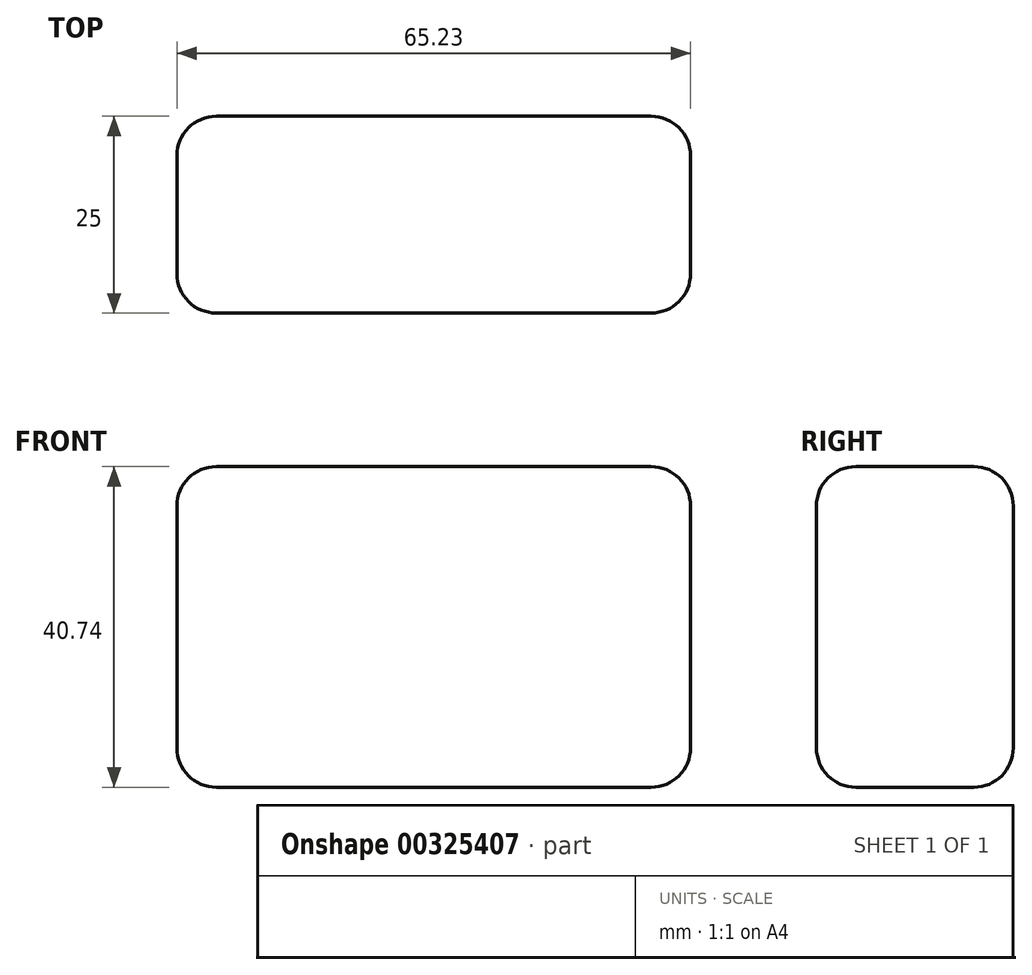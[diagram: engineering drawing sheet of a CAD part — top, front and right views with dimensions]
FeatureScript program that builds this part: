
annotation { "Feature Type Name" : "Feature", "Feature Type Description" : "" }
export const myFeature = defineFeature(function(context is Context, id is Id, definition is map)
    precondition{}
    {
        {
            var Q0;
            Q0=qCreatedBy(makeId("Front.planeOp"),FACE);
            var sketch = newSketch(context, id + "F0", { "sketchPlane" : qUnion([Q0])});
            skLineSegment(sketch, "E0.bottom", {"start": v(18.75, 67.72) * mm, "end": v(83.98, 67.72) * mm});
            skLineSegment(sketch, "E0.top", {"start": v(18.75, 26.98) * mm, "end": v(83.98, 26.98) * mm});
            skLineSegment(sketch, "E0.left", {"start": v(18.75, 67.72) * mm, "end": v(18.75, 26.98) * mm});
            skLineSegment(sketch, "E0.right", {"start": v(83.98, 67.72) * mm, "end": v(83.98, 26.98) * mm});
            skSolve(sketch);
        }
        {
            var Q0;
            Q0=makeQuery(id+"F0.imprint","IMPRINT",FACE,{"disambiguationData":[TD([[makeQuery(id+"F0.imprint","IMPRINT",EDGE,{"derivedFrom":sQuery(id+"F0.wireOp",EDGE,"E0.bottom")}),-1.0]])]});
            extrude(context, id + "F1", {"entities" : qUnion([Q0]), "depth" : 25 * mm});
        }
        {
            var Q0;
            Q0=makeQuery(id+"F1.opExtrude","CAP_FACE",FACE,{"disambiguationData":[OSD([sQuery(id+"F0.wireOp",EDGE,"E0.bottom"),sQuery(id+"F0.wireOp",EDGE,"E0.top"),sQuery(id+"F0.wireOp",EDGE,"E0.left"),sQuery(id+"F0.wireOp",EDGE,"E0.right")])],"isStart":false});
            var Q1;
            Q1=makeQuery(id+"F1.opExtrude","SWEPT_FACE",FACE,{"disambiguationData":[OSD([sQuery(id+"F0.wireOp",EDGE,"E0.bottom")])]});
            var Q2;
            Q2=makeQuery(id+"F1.opExtrude","CAP_FACE",FACE,{"disambiguationData":[OSD([sQuery(id+"F0.wireOp",EDGE,"E0.bottom"),sQuery(id+"F0.wireOp",EDGE,"E0.top"),sQuery(id+"F0.wireOp",EDGE,"E0.left"),sQuery(id+"F0.wireOp",EDGE,"E0.right")])],"isStart":true});
            var Q3;
            Q3=makeQuery(id+"F1.opExtrude","SWEPT_FACE",FACE,{"disambiguationData":[OSD([sQuery(id+"F0.wireOp",EDGE,"E0.top")])]});
            fillet(context, id + "F2", {"entities" : qUnion([Q0, Q1, Q2, Q3]), "radius" : 5 * mm, "tangentPropagation" : true, "allowEdgeOverflow" : false});
        }
    });
